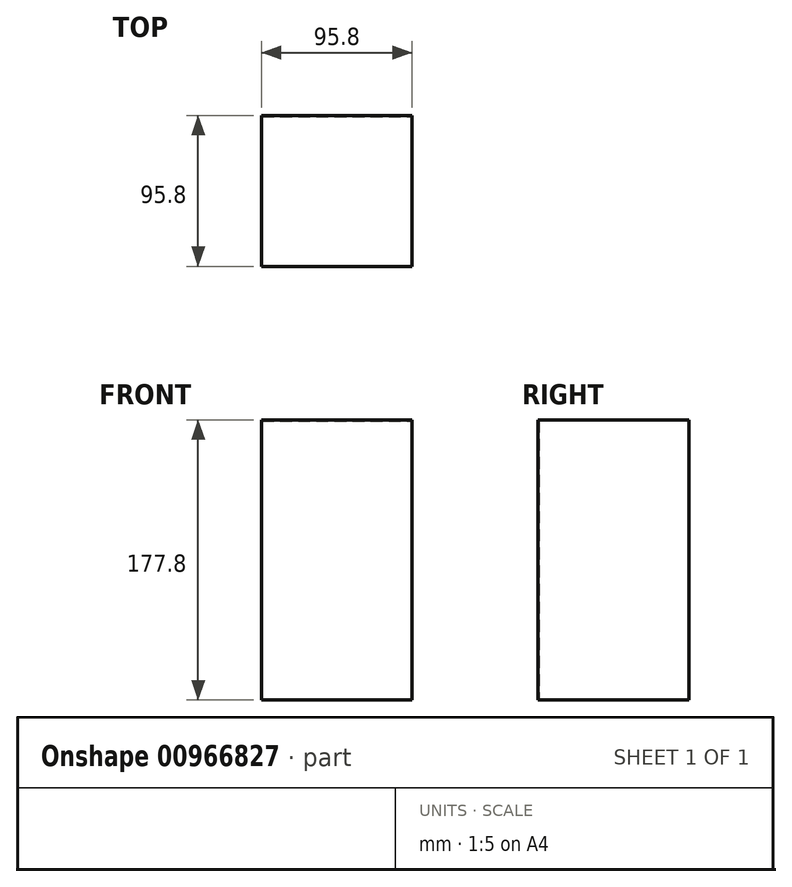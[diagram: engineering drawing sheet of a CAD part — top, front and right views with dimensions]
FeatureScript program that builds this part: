
annotation { "Feature Type Name" : "Feature", "Feature Type Description" : "" }
export const myFeature = defineFeature(function(context is Context, id is Id, definition is map)
    precondition{}
    {
        {
            var Q0;
            Q0=qCreatedBy(makeId("Top.planeOp"),FACE);
            var sketch = newSketch(context, id + "F0", { "sketchPlane" : qUnion([Q0])});
            skLineSegment(sketch, "E0.bottom", {"start": v(-47.9, 47.9) * mm, "end": v(47.9, 47.9) * mm});
            skLineSegment(sketch, "E0.top", {"start": v(-47.9, -47.9) * mm, "end": v(47.9, -47.9) * mm});
            skLineSegment(sketch, "E0.left", {"start": v(-47.9, 47.9) * mm, "end": v(-47.9, -47.9) * mm});
            skLineSegment(sketch, "E0.right", {"start": v(47.9, 47.9) * mm, "end": v(47.9, -47.9) * mm});
            skSolve(sketch);
        }
        {
            var Q0;
            Q0 = qSketchRegion(id + "F0", true);
            extrude(context, id + "F1", {"entities" : qUnion([Q0]), "endBound" : BoundingType.SYMMETRIC, "depth" : 177.8 * mm, "offsetDistance" : 25 * mm});
        }
        {
            var Q0;
            Q0=makeQuery(id+"F1.opExtrude","CAP_FACE",FACE,{"disambiguationData":[OSD([sQuery(id+"F0.wireOp",EDGE,"E0.bottom"),sQuery(id+"F0.wireOp",EDGE,"E0.top"),sQuery(id+"F0.wireOp",EDGE,"E0.left"),sQuery(id+"F0.wireOp",EDGE,"E0.right")])],"isStart":true});
            shell(context, id + "F2", {"entities" : qUnion([Q0]), "thickness" : 0.5 * mm});
        }
    });
